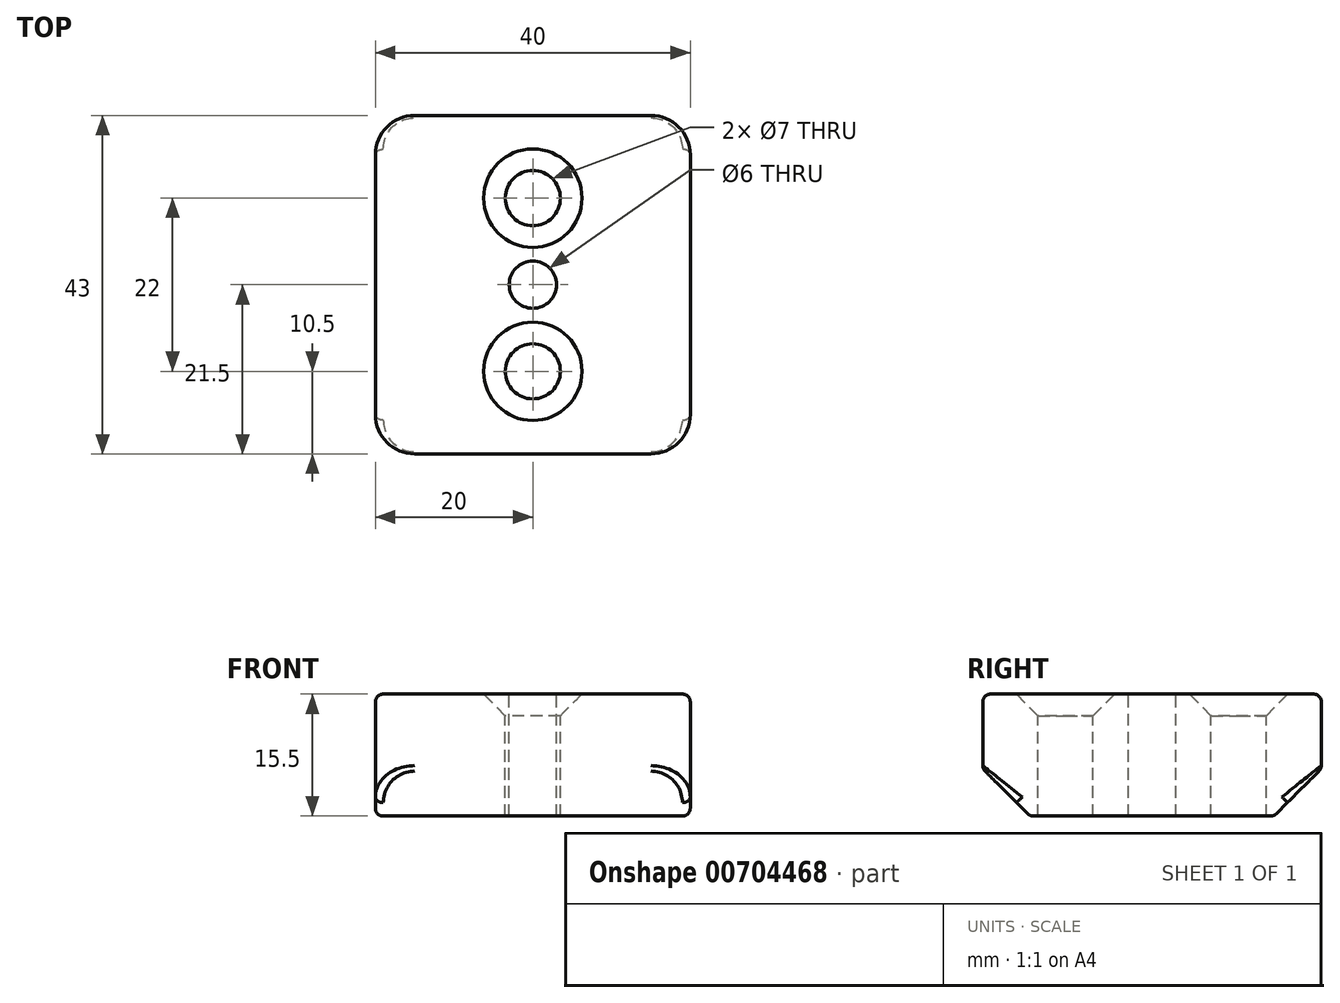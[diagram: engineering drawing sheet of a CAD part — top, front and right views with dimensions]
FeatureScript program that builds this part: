
annotation { "Feature Type Name" : "Feature", "Feature Type Description" : "" }
export const myFeature = defineFeature(function(context is Context, id is Id, definition is map)
    precondition{}
    {
        {
            var Q0;
            Q0=qCreatedBy(makeId("Top.planeOp"),FACE);
            var sketch = newSketch(context, id + "F0", { "sketchPlane" : qUnion([Q0])});
            skLineSegment(sketch, "E0.bottom", {"start": v(20, 21.5) * mm, "end": v(-20, 21.5) * mm});
            skLineSegment(sketch, "E0.top", {"start": v(20, -21.5) * mm, "end": v(-20, -21.5) * mm});
            skLineSegment(sketch, "E0.left", {"start": v(20, 21.5) * mm, "end": v(20, -21.5) * mm});
            skLineSegment(sketch, "E0.right", {"start": v(-20, 21.5) * mm, "end": v(-20, -21.5) * mm});
            skPoint(sketch, "E0.middle", {"position": v(0, 0) * mm});
            skCircle(sketch, "E1", {"center": v(0, 0) * mm, "radius": 3 * mm});
            skCircle(sketch, "E2", {"center": v(0, 11) * mm, "radius": 3.5 * mm});
            skCircle(sketch, "E3.MirrorC", {"center": v(0, -11) * mm, "radius": 3.5 * mm});
            skSolve(sketch);
        }
        {
            var Q0;
            Q0=makeQuery(id+"F0.imprint","IMPRINT",FACE,{"disambiguationData":[TD([[makeQuery(id+"F0.imprint","IMPRINT",EDGE,{"derivedFrom":sQuery(id+"F0.wireOp",EDGE,"E0.bottom")}),1.0]])]});
            extrude(context, id + "F1", {"entities" : qUnion([Q0]), "oppositeDirection" : true, "depth" : 15.5 * mm, "offsetDistance" : 25 * mm});
        }
        {
            var Q0;
            Q0=makeQuery(id+"F1.opExtrude","CAP_EDGE",EDGE,{"disambiguationData":[OSD([sQuery(id+"F0.wireOp",EDGE,"E3.MirrorC")])],"isStart":true});
            var Q1;
            Q1=makeQuery(id+"F1.opExtrude","CAP_EDGE",EDGE,{"disambiguationData":[OSD([sQuery(id+"F0.wireOp",EDGE,"E2")])],"isStart":true});
            chamfer(context, id + "F2", {"entities" : qUnion([Q0, Q1]), "width" : 2.75 * mm, "tangentPropagation" : true});
        }
        {
            var Q0;
            Q0=makeQuery(id+"F1.opExtrude","CAP_EDGE",EDGE,{"disambiguationData":[OSD([sQuery(id+"F0.wireOp",EDGE,"E0.top")])],"isStart":false});
            var Q1;
            Q1=makeQuery(id+"F1.opExtrude","CAP_EDGE",EDGE,{"disambiguationData":[OSD([sQuery(id+"F0.wireOp",EDGE,"E0.bottom")])],"isStart":false});
            chamfer(context, id + "F3", {"entities" : qUnion([Q0, Q1]), "width" : 6 * mm, "tangentPropagation" : true});
        }
        {
            var Q0;
            {var subQ0=sQuery(id+"F0.wireOp",EDGE,"E0.bottom");Q0=makeQuery(id+"F3.opChamfer","BLEND_EDGE",EDGE,{"blendedFrom":[makeQuery(id+"F1.opExtrude","CAP_EDGE",EDGE,{"disambiguationData":[OSD([subQ0])],"isStart":false}),makeQuery(id+"F1.opExtrude","CAP_FACE",FACE,{"disambiguationData":[OSD([subQ0,sQuery(id+"F0.wireOp",EDGE,"E0.top"),sQuery(id+"F0.wireOp",EDGE,"E0.left"),sQuery(id+"F0.wireOp",EDGE,"E0.right"),sQuery(id+"F0.wireOp",EDGE,"E1"),sQuery(id+"F0.wireOp",EDGE,"E2"),sQuery(id+"F0.wireOp",EDGE,"E3.MirrorC")])],"isStart":false})],"blendedInto":[makeQuery(id+"F1.opExtrude","CAP_FACE",FACE,{"disambiguationData":[OSD([subQ0,sQuery(id+"F0.wireOp",EDGE,"E0.top"),sQuery(id+"F0.wireOp",EDGE,"E0.left"),sQuery(id+"F0.wireOp",EDGE,"E0.right"),sQuery(id+"F0.wireOp",EDGE,"E1"),sQuery(id+"F0.wireOp",EDGE,"E2"),sQuery(id+"F0.wireOp",EDGE,"E3.MirrorC")])],"isStart":false})]});}
            var Q1;
            {var subQ0=sQuery(id+"F0.wireOp",EDGE,"E0.top");Q1=makeQuery(id+"F3.opChamfer","BLEND_EDGE",EDGE,{"blendedFrom":[makeQuery(id+"F1.opExtrude","CAP_EDGE",EDGE,{"disambiguationData":[OSD([subQ0])],"isStart":false}),makeQuery(id+"F1.opExtrude","CAP_FACE",FACE,{"disambiguationData":[OSD([sQuery(id+"F0.wireOp",EDGE,"E0.bottom"),subQ0,sQuery(id+"F0.wireOp",EDGE,"E0.left"),sQuery(id+"F0.wireOp",EDGE,"E0.right"),sQuery(id+"F0.wireOp",EDGE,"E1"),sQuery(id+"F0.wireOp",EDGE,"E2"),sQuery(id+"F0.wireOp",EDGE,"E3.MirrorC")])],"isStart":false})],"blendedInto":[makeQuery(id+"F1.opExtrude","CAP_FACE",FACE,{"disambiguationData":[OSD([sQuery(id+"F0.wireOp",EDGE,"E0.bottom"),subQ0,sQuery(id+"F0.wireOp",EDGE,"E0.left"),sQuery(id+"F0.wireOp",EDGE,"E0.right"),sQuery(id+"F0.wireOp",EDGE,"E1"),sQuery(id+"F0.wireOp",EDGE,"E2"),sQuery(id+"F0.wireOp",EDGE,"E3.MirrorC")])],"isStart":false})]});}
            fillet(context, id + "F4", {"entities" : qUnion([Q0, Q1]), "radius" : 1 * mm, "tangentPropagation" : true, "allowEdgeOverflow" : false});
        }
        {
            var Q0;
            Q0=makeQuery(id+"F1.opExtrude","SWEPT_EDGE",EDGE,{"disambiguationData":[OSD([sQuery(id+"F0.wireOp",EDGE,"E0.bottom"),sQuery(id+"F0.wireOp",EDGE,"E0.right")])]});
            var Q1;
            Q1=makeQuery(id+"F1.opExtrude","SWEPT_EDGE",EDGE,{"disambiguationData":[OSD([sQuery(id+"F0.wireOp",EDGE,"E0.bottom"),sQuery(id+"F0.wireOp",EDGE,"E0.left")])]});
            var Q2;
            Q2=makeQuery(id+"F1.opExtrude","SWEPT_EDGE",EDGE,{"disambiguationData":[OSD([sQuery(id+"F0.wireOp",EDGE,"E0.top"),sQuery(id+"F0.wireOp",EDGE,"E0.right")])]});
            var Q3;
            Q3=makeQuery(id+"F1.opExtrude","SWEPT_EDGE",EDGE,{"disambiguationData":[OSD([sQuery(id+"F0.wireOp",EDGE,"E0.top"),sQuery(id+"F0.wireOp",EDGE,"E0.left")])]});
            fillet(context, id + "F5", {"entities" : qUnion([Q0, Q1, Q2, Q3]), "radius" : 5 * mm, "tangentPropagation" : true, "allowEdgeOverflow" : false});
        }
        {
            var Q0;
            Q0=makeQuery(id+"F1.opExtrude","CAP_EDGE",EDGE,{"disambiguationData":[OSD([sQuery(id+"F0.wireOp",EDGE,"E0.right")])],"isStart":false});
            var Q1;
            {var subQ0=sQuery(id+"F0.wireOp",EDGE,"E0.right");var subQ1=sQuery(id+"F0.wireOp",EDGE,"E0.bottom");Q1=makeQuery(id+"F4.opFillet","BLEND_EDGE",EDGE,{"blendedFrom":[makeQuery(id+"F3.opChamfer","BLEND_EDGE",EDGE,{"blendedFrom":[makeQuery(id+"F1.opExtrude","CAP_EDGE",EDGE,{"disambiguationData":[OSD([subQ1])],"isStart":false}),makeQuery(id+"F1.opExtrude","CAP_FACE",FACE,{"disambiguationData":[OSD([subQ1,sQuery(id+"F0.wireOp",EDGE,"E0.top"),sQuery(id+"F0.wireOp",EDGE,"E0.left"),subQ0,sQuery(id+"F0.wireOp",EDGE,"E1"),sQuery(id+"F0.wireOp",EDGE,"E2"),sQuery(id+"F0.wireOp",EDGE,"E3.MirrorC")])],"isStart":false})],"blendedInto":[makeQuery(id+"F1.opExtrude","CAP_FACE",FACE,{"disambiguationData":[OSD([subQ1,sQuery(id+"F0.wireOp",EDGE,"E0.top"),sQuery(id+"F0.wireOp",EDGE,"E0.left"),subQ0,sQuery(id+"F0.wireOp",EDGE,"E1"),sQuery(id+"F0.wireOp",EDGE,"E2"),sQuery(id+"F0.wireOp",EDGE,"E3.MirrorC")])],"isStart":false})]}),makeQuery(id+"F1.opExtrude","SWEPT_FACE",FACE,{"disambiguationData":[OSD([subQ0])]})],"blendedInto":[makeQuery(id+"F1.opExtrude","SWEPT_FACE",FACE,{"disambiguationData":[OSD([subQ0])]})]});}
            var Q2;
            Q2=makeQuery(id+"F3.opChamfer","BLEND_EDGE",EDGE,{"blendedFrom":[makeQuery(id+"F1.opExtrude","CAP_EDGE",EDGE,{"disambiguationData":[OSD([sQuery(id+"F0.wireOp",EDGE,"E0.bottom")])],"isStart":false}),makeQuery(id+"F1.opExtrude","SWEPT_FACE",FACE,{"disambiguationData":[OSD([sQuery(id+"F0.wireOp",EDGE,"E0.right")])]})],"blendedInto":[makeQuery(id+"F1.opExtrude","SWEPT_FACE",FACE,{"disambiguationData":[OSD([sQuery(id+"F0.wireOp",EDGE,"E0.right")])]})]});
            var Q3;
            {var subQ0=sQuery(id+"F0.wireOp",EDGE,"E0.bottom");Q3=makeQuery(id+"F5.opFillet","BLEND_EDGE",EDGE,{"blendedFrom":[makeQuery(id+"F1.opExtrude","SWEPT_EDGE",EDGE,{"disambiguationData":[OSD([subQ0,sQuery(id+"F0.wireOp",EDGE,"E0.right")])]}),makeQuery(id+"F3.opChamfer","BLEND_FACE",FACE,{"disambiguationData":[OSD([subQ0])]})],"blendedInto":[makeQuery(id+"F3.opChamfer","BLEND_FACE",FACE,{"disambiguationData":[OSD([subQ0])]})]});}
            var Q4;
            {var subQ0=sQuery(id+"F0.wireOp",EDGE,"E0.bottom");Q4=makeQuery(id+"F3.opChamfer","BLEND_EDGE",EDGE,{"blendedFrom":[makeQuery(id+"F1.opExtrude","CAP_EDGE",EDGE,{"disambiguationData":[OSD([subQ0])],"isStart":false}),makeQuery(id+"F1.opExtrude","SWEPT_FACE",FACE,{"disambiguationData":[OSD([subQ0])]})],"blendedInto":[makeQuery(id+"F1.opExtrude","SWEPT_FACE",FACE,{"disambiguationData":[OSD([subQ0])]})]});}
            var Q5;
            {var subQ0=sQuery(id+"F0.wireOp",EDGE,"E0.right");var subQ1=sQuery(id+"F0.wireOp",EDGE,"E0.top");Q5=makeQuery(id+"F4.opFillet","BLEND_EDGE",EDGE,{"blendedFrom":[makeQuery(id+"F3.opChamfer","BLEND_EDGE",EDGE,{"blendedFrom":[makeQuery(id+"F1.opExtrude","CAP_EDGE",EDGE,{"disambiguationData":[OSD([subQ1])],"isStart":false}),makeQuery(id+"F1.opExtrude","CAP_FACE",FACE,{"disambiguationData":[OSD([sQuery(id+"F0.wireOp",EDGE,"E0.bottom"),subQ1,sQuery(id+"F0.wireOp",EDGE,"E0.left"),subQ0,sQuery(id+"F0.wireOp",EDGE,"E1"),sQuery(id+"F0.wireOp",EDGE,"E2"),sQuery(id+"F0.wireOp",EDGE,"E3.MirrorC")])],"isStart":false})],"blendedInto":[makeQuery(id+"F1.opExtrude","CAP_FACE",FACE,{"disambiguationData":[OSD([sQuery(id+"F0.wireOp",EDGE,"E0.bottom"),subQ1,sQuery(id+"F0.wireOp",EDGE,"E0.left"),subQ0,sQuery(id+"F0.wireOp",EDGE,"E1"),sQuery(id+"F0.wireOp",EDGE,"E2"),sQuery(id+"F0.wireOp",EDGE,"E3.MirrorC")])],"isStart":false})]}),makeQuery(id+"F1.opExtrude","SWEPT_FACE",FACE,{"disambiguationData":[OSD([subQ0])]})],"blendedInto":[makeQuery(id+"F1.opExtrude","SWEPT_FACE",FACE,{"disambiguationData":[OSD([subQ0])]})]});}
            var Q6;
            Q6=makeQuery(id+"F3.opChamfer","BLEND_EDGE",EDGE,{"blendedFrom":[makeQuery(id+"F1.opExtrude","CAP_EDGE",EDGE,{"disambiguationData":[OSD([sQuery(id+"F0.wireOp",EDGE,"E0.top")])],"isStart":false}),makeQuery(id+"F1.opExtrude","SWEPT_FACE",FACE,{"disambiguationData":[OSD([sQuery(id+"F0.wireOp",EDGE,"E0.right")])]})],"blendedInto":[makeQuery(id+"F1.opExtrude","SWEPT_FACE",FACE,{"disambiguationData":[OSD([sQuery(id+"F0.wireOp",EDGE,"E0.right")])]})]});
            var Q7;
            {var subQ0=sQuery(id+"F0.wireOp",EDGE,"E0.top");Q7=makeQuery(id+"F5.opFillet","BLEND_EDGE",EDGE,{"blendedFrom":[makeQuery(id+"F1.opExtrude","SWEPT_EDGE",EDGE,{"disambiguationData":[OSD([subQ0,sQuery(id+"F0.wireOp",EDGE,"E0.right")])]}),makeQuery(id+"F3.opChamfer","BLEND_FACE",FACE,{"disambiguationData":[OSD([subQ0])]})],"blendedInto":[makeQuery(id+"F3.opChamfer","BLEND_FACE",FACE,{"disambiguationData":[OSD([subQ0])]})]});}
            var Q8;
            {var subQ0=sQuery(id+"F0.wireOp",EDGE,"E0.top");Q8=makeQuery(id+"F3.opChamfer","BLEND_EDGE",EDGE,{"blendedFrom":[makeQuery(id+"F1.opExtrude","CAP_EDGE",EDGE,{"disambiguationData":[OSD([subQ0])],"isStart":false}),makeQuery(id+"F1.opExtrude","SWEPT_FACE",FACE,{"disambiguationData":[OSD([subQ0])]})],"blendedInto":[makeQuery(id+"F1.opExtrude","SWEPT_FACE",FACE,{"disambiguationData":[OSD([subQ0])]})]});}
            var Q9;
            {var subQ0=sQuery(id+"F0.wireOp",EDGE,"E0.bottom");Q9=makeQuery(id+"F5.opFillet","BLEND_EDGE",EDGE,{"blendedFrom":[makeQuery(id+"F1.opExtrude","SWEPT_EDGE",EDGE,{"disambiguationData":[OSD([subQ0,sQuery(id+"F0.wireOp",EDGE,"E0.left")])]}),makeQuery(id+"F3.opChamfer","BLEND_FACE",FACE,{"disambiguationData":[OSD([subQ0])]})],"blendedInto":[makeQuery(id+"F3.opChamfer","BLEND_FACE",FACE,{"disambiguationData":[OSD([subQ0])]})]});}
            var Q10;
            Q10=makeQuery(id+"F3.opChamfer","BLEND_EDGE",EDGE,{"blendedFrom":[makeQuery(id+"F1.opExtrude","CAP_EDGE",EDGE,{"disambiguationData":[OSD([sQuery(id+"F0.wireOp",EDGE,"E0.bottom")])],"isStart":false}),makeQuery(id+"F1.opExtrude","SWEPT_FACE",FACE,{"disambiguationData":[OSD([sQuery(id+"F0.wireOp",EDGE,"E0.left")])]})],"blendedInto":[makeQuery(id+"F1.opExtrude","SWEPT_FACE",FACE,{"disambiguationData":[OSD([sQuery(id+"F0.wireOp",EDGE,"E0.left")])]})]});
            var Q11;
            {var subQ0=sQuery(id+"F0.wireOp",EDGE,"E0.left");var subQ1=sQuery(id+"F0.wireOp",EDGE,"E0.bottom");Q11=makeQuery(id+"F4.opFillet","BLEND_EDGE",EDGE,{"blendedFrom":[makeQuery(id+"F3.opChamfer","BLEND_EDGE",EDGE,{"blendedFrom":[makeQuery(id+"F1.opExtrude","CAP_EDGE",EDGE,{"disambiguationData":[OSD([subQ1])],"isStart":false}),makeQuery(id+"F1.opExtrude","CAP_FACE",FACE,{"disambiguationData":[OSD([subQ1,sQuery(id+"F0.wireOp",EDGE,"E0.top"),subQ0,sQuery(id+"F0.wireOp",EDGE,"E0.right"),sQuery(id+"F0.wireOp",EDGE,"E1"),sQuery(id+"F0.wireOp",EDGE,"E2"),sQuery(id+"F0.wireOp",EDGE,"E3.MirrorC")])],"isStart":false})],"blendedInto":[makeQuery(id+"F1.opExtrude","CAP_FACE",FACE,{"disambiguationData":[OSD([subQ1,sQuery(id+"F0.wireOp",EDGE,"E0.top"),subQ0,sQuery(id+"F0.wireOp",EDGE,"E0.right"),sQuery(id+"F0.wireOp",EDGE,"E1"),sQuery(id+"F0.wireOp",EDGE,"E2"),sQuery(id+"F0.wireOp",EDGE,"E3.MirrorC")])],"isStart":false})]}),makeQuery(id+"F1.opExtrude","SWEPT_FACE",FACE,{"disambiguationData":[OSD([subQ0])]})],"blendedInto":[makeQuery(id+"F1.opExtrude","SWEPT_FACE",FACE,{"disambiguationData":[OSD([subQ0])]})]});}
            var Q12;
            Q12=makeQuery(id+"F1.opExtrude","CAP_EDGE",EDGE,{"disambiguationData":[OSD([sQuery(id+"F0.wireOp",EDGE,"E0.left")])],"isStart":false});
            var Q13;
            {var subQ0=sQuery(id+"F0.wireOp",EDGE,"E0.left");var subQ1=sQuery(id+"F0.wireOp",EDGE,"E0.top");Q13=makeQuery(id+"F4.opFillet","BLEND_EDGE",EDGE,{"blendedFrom":[makeQuery(id+"F3.opChamfer","BLEND_EDGE",EDGE,{"blendedFrom":[makeQuery(id+"F1.opExtrude","CAP_EDGE",EDGE,{"disambiguationData":[OSD([subQ1])],"isStart":false}),makeQuery(id+"F1.opExtrude","CAP_FACE",FACE,{"disambiguationData":[OSD([sQuery(id+"F0.wireOp",EDGE,"E0.bottom"),subQ1,subQ0,sQuery(id+"F0.wireOp",EDGE,"E0.right"),sQuery(id+"F0.wireOp",EDGE,"E1"),sQuery(id+"F0.wireOp",EDGE,"E2"),sQuery(id+"F0.wireOp",EDGE,"E3.MirrorC")])],"isStart":false})],"blendedInto":[makeQuery(id+"F1.opExtrude","CAP_FACE",FACE,{"disambiguationData":[OSD([sQuery(id+"F0.wireOp",EDGE,"E0.bottom"),subQ1,subQ0,sQuery(id+"F0.wireOp",EDGE,"E0.right"),sQuery(id+"F0.wireOp",EDGE,"E1"),sQuery(id+"F0.wireOp",EDGE,"E2"),sQuery(id+"F0.wireOp",EDGE,"E3.MirrorC")])],"isStart":false})]}),makeQuery(id+"F1.opExtrude","SWEPT_FACE",FACE,{"disambiguationData":[OSD([subQ0])]})],"blendedInto":[makeQuery(id+"F1.opExtrude","SWEPT_FACE",FACE,{"disambiguationData":[OSD([subQ0])]})]});}
            var Q14;
            Q14=makeQuery(id+"F3.opChamfer","BLEND_EDGE",EDGE,{"blendedFrom":[makeQuery(id+"F1.opExtrude","CAP_EDGE",EDGE,{"disambiguationData":[OSD([sQuery(id+"F0.wireOp",EDGE,"E0.top")])],"isStart":false}),makeQuery(id+"F1.opExtrude","SWEPT_FACE",FACE,{"disambiguationData":[OSD([sQuery(id+"F0.wireOp",EDGE,"E0.left")])]})],"blendedInto":[makeQuery(id+"F1.opExtrude","SWEPT_FACE",FACE,{"disambiguationData":[OSD([sQuery(id+"F0.wireOp",EDGE,"E0.left")])]})]});
            var Q15;
            {var subQ0=sQuery(id+"F0.wireOp",EDGE,"E0.top");Q15=makeQuery(id+"F5.opFillet","BLEND_EDGE",EDGE,{"blendedFrom":[makeQuery(id+"F1.opExtrude","SWEPT_EDGE",EDGE,{"disambiguationData":[OSD([subQ0,sQuery(id+"F0.wireOp",EDGE,"E0.left")])]}),makeQuery(id+"F3.opChamfer","BLEND_FACE",FACE,{"disambiguationData":[OSD([subQ0])]})],"blendedInto":[makeQuery(id+"F3.opChamfer","BLEND_FACE",FACE,{"disambiguationData":[OSD([subQ0])]})]});}
            fillet(context, id + "F6", {"entities" : qUnion([Q0, Q1, Q2, Q3, Q4, Q5, Q6, Q7, Q8, Q9, Q10, Q11, Q12, Q13, Q14, Q15]), "radius" : 1 * mm, "tangentPropagation" : true, "allowEdgeOverflow" : false});
        }
        {
            var Q0;
            {var subQ0=sQuery(id+"F0.wireOp",EDGE,"E0.right");var subQ1=sQuery(id+"F0.wireOp",EDGE,"E0.bottom");Q0=makeQuery(id+"F5.opFillet","BLEND_EDGE",EDGE,{"blendedFrom":[makeQuery(id+"F1.opExtrude","SWEPT_EDGE",EDGE,{"disambiguationData":[OSD([subQ1,subQ0])]}),makeQuery(id+"F1.opExtrude","CAP_FACE",FACE,{"disambiguationData":[OSD([subQ1,sQuery(id+"F0.wireOp",EDGE,"E0.top"),sQuery(id+"F0.wireOp",EDGE,"E0.left"),subQ0,sQuery(id+"F0.wireOp",EDGE,"E1"),sQuery(id+"F0.wireOp",EDGE,"E2"),sQuery(id+"F0.wireOp",EDGE,"E3.MirrorC")])],"isStart":true})],"blendedInto":[makeQuery(id+"F1.opExtrude","CAP_FACE",FACE,{"disambiguationData":[OSD([subQ1,sQuery(id+"F0.wireOp",EDGE,"E0.top"),sQuery(id+"F0.wireOp",EDGE,"E0.left"),subQ0,sQuery(id+"F0.wireOp",EDGE,"E1"),sQuery(id+"F0.wireOp",EDGE,"E2"),sQuery(id+"F0.wireOp",EDGE,"E3.MirrorC")])],"isStart":true})]});}
            var Q1;
            Q1=makeQuery(id+"F1.opExtrude","CAP_EDGE",EDGE,{"disambiguationData":[OSD([sQuery(id+"F0.wireOp",EDGE,"E0.bottom")])],"isStart":true});
            var Q2;
            Q2=makeQuery(id+"F1.opExtrude","CAP_EDGE",EDGE,{"disambiguationData":[OSD([sQuery(id+"F0.wireOp",EDGE,"E0.right")])],"isStart":true});
            var Q3;
            {var subQ0=sQuery(id+"F0.wireOp",EDGE,"E0.right");var subQ1=sQuery(id+"F0.wireOp",EDGE,"E0.top");Q3=makeQuery(id+"F5.opFillet","BLEND_EDGE",EDGE,{"blendedFrom":[makeQuery(id+"F1.opExtrude","SWEPT_EDGE",EDGE,{"disambiguationData":[OSD([subQ1,subQ0])]}),makeQuery(id+"F1.opExtrude","CAP_FACE",FACE,{"disambiguationData":[OSD([sQuery(id+"F0.wireOp",EDGE,"E0.bottom"),subQ1,sQuery(id+"F0.wireOp",EDGE,"E0.left"),subQ0,sQuery(id+"F0.wireOp",EDGE,"E1"),sQuery(id+"F0.wireOp",EDGE,"E2"),sQuery(id+"F0.wireOp",EDGE,"E3.MirrorC")])],"isStart":true})],"blendedInto":[makeQuery(id+"F1.opExtrude","CAP_FACE",FACE,{"disambiguationData":[OSD([sQuery(id+"F0.wireOp",EDGE,"E0.bottom"),subQ1,sQuery(id+"F0.wireOp",EDGE,"E0.left"),subQ0,sQuery(id+"F0.wireOp",EDGE,"E1"),sQuery(id+"F0.wireOp",EDGE,"E2"),sQuery(id+"F0.wireOp",EDGE,"E3.MirrorC")])],"isStart":true})]});}
            var Q4;
            Q4=makeQuery(id+"F1.opExtrude","CAP_EDGE",EDGE,{"disambiguationData":[OSD([sQuery(id+"F0.wireOp",EDGE,"E0.top")])],"isStart":true});
            var Q5;
            {var subQ0=sQuery(id+"F0.wireOp",EDGE,"E0.left");var subQ1=sQuery(id+"F0.wireOp",EDGE,"E0.top");Q5=makeQuery(id+"F5.opFillet","BLEND_EDGE",EDGE,{"blendedFrom":[makeQuery(id+"F1.opExtrude","SWEPT_EDGE",EDGE,{"disambiguationData":[OSD([subQ1,subQ0])]}),makeQuery(id+"F1.opExtrude","CAP_FACE",FACE,{"disambiguationData":[OSD([sQuery(id+"F0.wireOp",EDGE,"E0.bottom"),subQ1,subQ0,sQuery(id+"F0.wireOp",EDGE,"E0.right"),sQuery(id+"F0.wireOp",EDGE,"E1"),sQuery(id+"F0.wireOp",EDGE,"E2"),sQuery(id+"F0.wireOp",EDGE,"E3.MirrorC")])],"isStart":true})],"blendedInto":[makeQuery(id+"F1.opExtrude","CAP_FACE",FACE,{"disambiguationData":[OSD([sQuery(id+"F0.wireOp",EDGE,"E0.bottom"),subQ1,subQ0,sQuery(id+"F0.wireOp",EDGE,"E0.right"),sQuery(id+"F0.wireOp",EDGE,"E1"),sQuery(id+"F0.wireOp",EDGE,"E2"),sQuery(id+"F0.wireOp",EDGE,"E3.MirrorC")])],"isStart":true})]});}
            var Q6;
            Q6=makeQuery(id+"F1.opExtrude","CAP_EDGE",EDGE,{"disambiguationData":[OSD([sQuery(id+"F0.wireOp",EDGE,"E0.left")])],"isStart":true});
            var Q7;
            {var subQ0=sQuery(id+"F0.wireOp",EDGE,"E0.left");var subQ1=sQuery(id+"F0.wireOp",EDGE,"E0.bottom");Q7=makeQuery(id+"F5.opFillet","BLEND_EDGE",EDGE,{"blendedFrom":[makeQuery(id+"F1.opExtrude","SWEPT_EDGE",EDGE,{"disambiguationData":[OSD([subQ1,subQ0])]}),makeQuery(id+"F1.opExtrude","CAP_FACE",FACE,{"disambiguationData":[OSD([subQ1,sQuery(id+"F0.wireOp",EDGE,"E0.top"),subQ0,sQuery(id+"F0.wireOp",EDGE,"E0.right"),sQuery(id+"F0.wireOp",EDGE,"E1"),sQuery(id+"F0.wireOp",EDGE,"E2"),sQuery(id+"F0.wireOp",EDGE,"E3.MirrorC")])],"isStart":true})],"blendedInto":[makeQuery(id+"F1.opExtrude","CAP_FACE",FACE,{"disambiguationData":[OSD([subQ1,sQuery(id+"F0.wireOp",EDGE,"E0.top"),subQ0,sQuery(id+"F0.wireOp",EDGE,"E0.right"),sQuery(id+"F0.wireOp",EDGE,"E1"),sQuery(id+"F0.wireOp",EDGE,"E2"),sQuery(id+"F0.wireOp",EDGE,"E3.MirrorC")])],"isStart":true})]});}
            fillet(context, id + "F7", {"entities" : qUnion([Q0, Q1, Q2, Q3, Q4, Q5, Q6, Q7]), "radius" : 1 * mm, "tangentPropagation" : true, "allowEdgeOverflow" : false});
        }
    });
